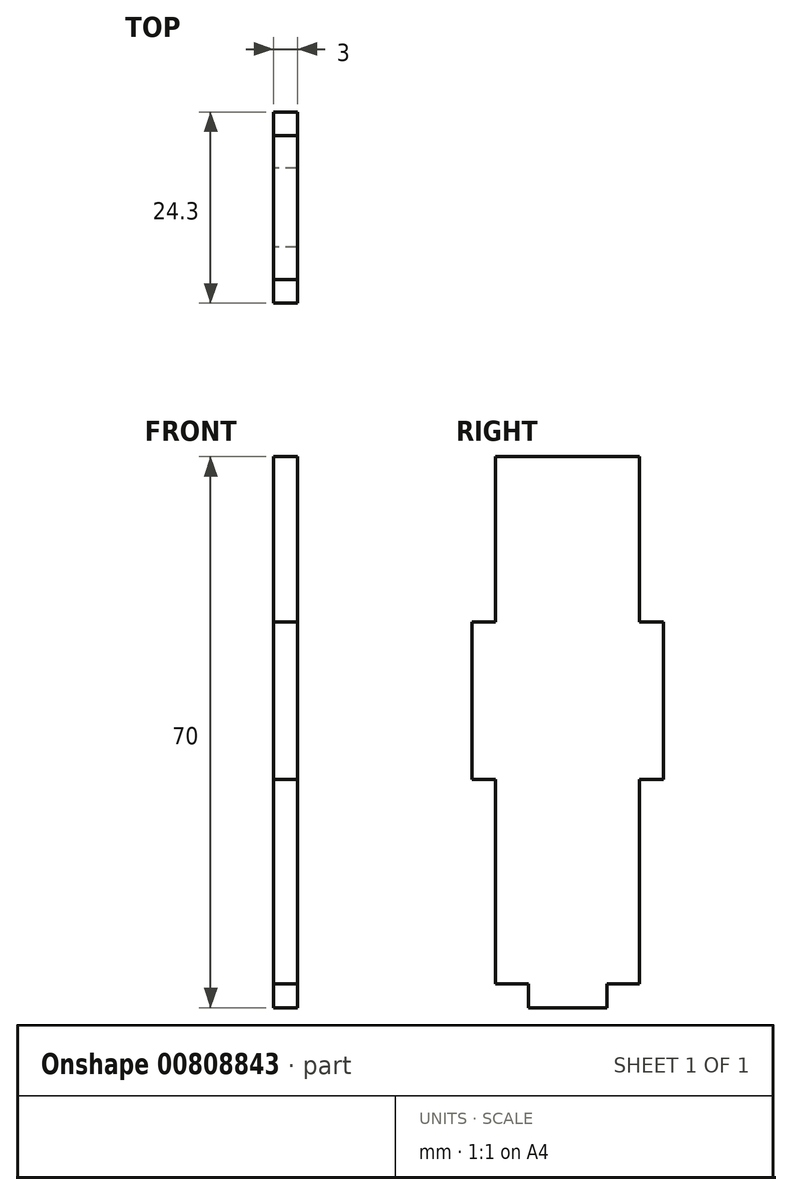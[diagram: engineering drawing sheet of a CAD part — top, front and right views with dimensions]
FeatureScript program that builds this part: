
annotation { "Feature Type Name" : "Feature", "Feature Type Description" : "" }
export const myFeature = defineFeature(function(context is Context, id is Id, definition is map)
    precondition{}
    {
        {
            var Q0;
            Q0=qCreatedBy(makeId("Right.planeOp"),FACE);
            var sketch = newSketch(context, id + "F0", { "sketchPlane" : qUnion([Q0])});
            skLineSegment(sketch, "E0.bottom", {"start": v(-9.15, -33.5) * mm, "end": v(9.15, -33.5) * mm});
            skLineSegment(sketch, "E0.top", {"start": v(-9.15, 33.5) * mm, "end": v(9.15, 33.5) * mm});
            skLineSegment(sketch, "E0.left", {"start": v(-9.15, -33.5) * mm, "end": v(-9.15, 33.5) * mm});
            skLineSegment(sketch, "E0.right", {"start": v(9.15, -33.5) * mm, "end": v(9.15, 33.5) * mm});
            skPoint(sketch, "E0.middle", {"position": v(0, 0) * mm});
            skLineSegment(sketch, "E1.bottom", {"start": v(12.15, -7.5) * mm, "end": v(6.15, -7.5) * mm});
            skLineSegment(sketch, "E1.top", {"start": v(12.15, 12.5) * mm, "end": v(6.15, 12.5) * mm});
            skLineSegment(sketch, "E1.left", {"start": v(12.15, -7.5) * mm, "end": v(12.15, 12.5) * mm});
            skLineSegment(sketch, "E1.right", {"start": v(6.15, -7.5) * mm, "end": v(6.15, 12.5) * mm});
            skPoint(sketch, "E1.middle", {"position": v(9.15, 2.5) * mm});
            skLineSegment(sketch, "E2.bottom", {"start": v(-12.15, -7.5) * mm, "end": v(-6.15, -7.5) * mm});
            skLineSegment(sketch, "E2.top", {"start": v(-12.15, 12.5) * mm, "end": v(-6.15, 12.5) * mm});
            skLineSegment(sketch, "E2.left", {"start": v(-12.15, -7.5) * mm, "end": v(-12.15, 12.5) * mm});
            skLineSegment(sketch, "E2.right", {"start": v(-6.15, -7.5) * mm, "end": v(-6.15, 12.5) * mm});
            skPoint(sketch, "E2.middle", {"position": v(-9.15, 2.5) * mm});
            skLineSegment(sketch, "E3.bottom", {"start": v(5, -36.5) * mm, "end": v(-5, -36.5) * mm});
            skLineSegment(sketch, "E3.top", {"start": v(5, -30.5) * mm, "end": v(-5, -30.5) * mm});
            skLineSegment(sketch, "E3.left", {"start": v(5, -36.5) * mm, "end": v(5, -30.5) * mm});
            skLineSegment(sketch, "E3.right", {"start": v(-5, -36.5) * mm, "end": v(-5, -30.5) * mm});
            skPoint(sketch, "E3.middle", {"position": v(0, -33.5) * mm});
            skSolve(sketch);
        }
        {
            var Q0;
            Q0=qSketchRegion(id+"F0",true);
            extrude(context, id + "F1", {"entities" : qUnion([Q0]), "depth" : 3 * mm, "offsetDistance" : 25 * mm});
        }
    });
